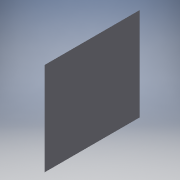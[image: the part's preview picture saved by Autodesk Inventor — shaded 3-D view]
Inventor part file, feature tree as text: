
AUTODESK INVENTOR PART (.ipt)
format: ipt  version: 2018 (Build 220112000, 112)  size: 94,720 bytes
history: native  units: mm
features: extrude x1, chamfer x1, sketch x1
ambient origin geometry x8: Origin, YZ Plane, XZ Plane, XY Plane, X Axis, Y Axis, Z Axis, Center Point
bodies: Volumenkörper1 (feature_tree)
feature tree (3):
  extrude  "Extrusion1"  Depth=20.0mm
  chamfer  "Fase1"  Distance=20.0mm
  sketch  "Skizze1"  dims[d0=440.0mm d1=450.0mm d2=20.0mm d3=0.0mm d4=20.0mm d5=2.0mm d6=45.0deg]
